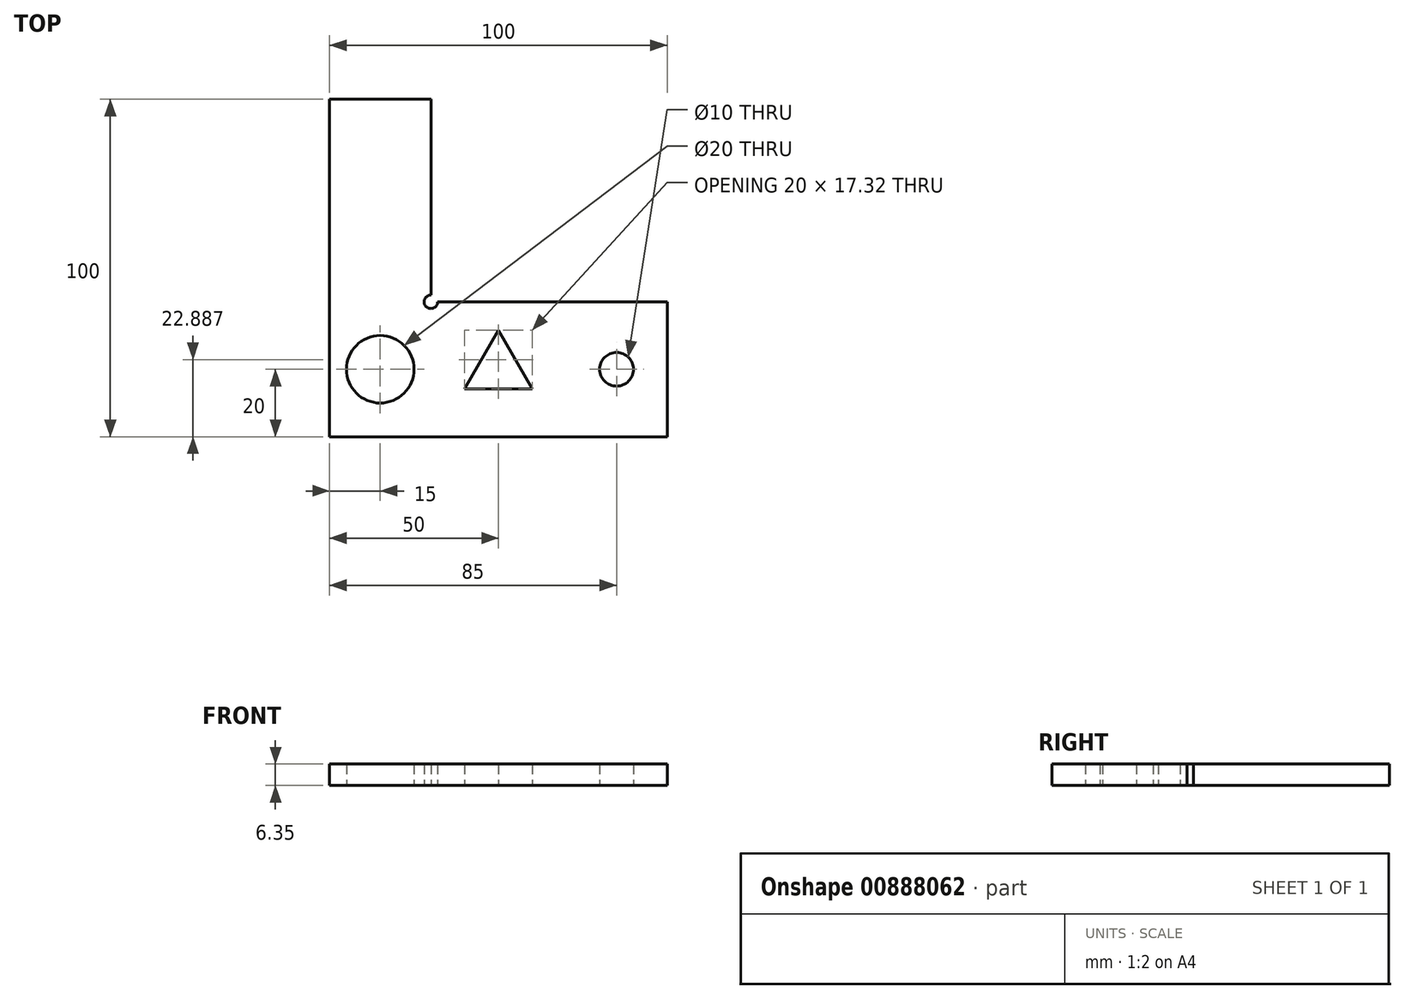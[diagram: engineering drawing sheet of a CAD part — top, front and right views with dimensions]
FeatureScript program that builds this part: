
annotation { "Feature Type Name" : "Feature", "Feature Type Description" : "" }
export const myFeature = defineFeature(function(context is Context, id is Id, definition is map)
    precondition{}
    {
        {
            var Q0;
            Q0=qCreatedBy(makeId("Top.planeOp"),FACE);
            var sketch = newSketch(context, id + "F0", { "sketchPlane" : qUnion([Q0])});
            skLineSegment(sketch, "E0", {"start": v(15, 80) * mm, "end": v(15, 22) * mm});
            skLineSegment(sketch, "E1", {"start": v(17, 20) * mm, "end": v(85, 20) * mm});
            skLineSegment(sketch, "E2", {"start": v(85, 20) * mm, "end": v(85, -20) * mm});
            skLineSegment(sketch, "E3", {"start": v(85, -20) * mm, "end": v(-15, -20) * mm});
            skLineSegment(sketch, "E4", {"start": v(-15, -20) * mm, "end": v(-15, 80) * mm});
            skLineSegment(sketch, "E5", {"start": v(-15, 80) * mm, "end": v(15, 80) * mm});
            skPoint(sketch, "E6", {"position": v(85, 0) * mm});
            skPoint(sketch, "E7", {"position": v(0, 80) * mm});
            skArc(sketch, "E8", {"start": v(17, 20) * mm, "mid": v(13.59, 18.59) * mm, "end": v(15, 22) * mm});
            skCircle(sketch, "E9", {"center": v(0, 0) * mm, "radius": 10 * mm});
            skCircle(sketch, "E10", {"center": v(70, 0) * mm, "radius": 5 * mm});
            skLineSegment(sketch, "E11", {"start": v(0, 0) * mm, "end": v(70, 0) * mm, "construction": true});
            skLineSegment(sketch, "E12", {"start": v(85, 0) * mm, "end": v(70, 0) * mm, "construction": true});
            skCircle(sketch, "E13.cCircle", {"center": v(35, 0) * mm, "radius": 5.77 * mm, "construction": true});
            skLineSegment(sketch, "E13.0", {"start": v(35, 11.55) * mm, "end": v(45, -5.77) * mm});
            skLineSegment(sketch, "E13.1", {"start": v(45, -5.77) * mm, "end": v(25, -5.77) * mm});
            skLineSegment(sketch, "E13.2", {"start": v(25, -5.77) * mm, "end": v(35, 11.55) * mm});
            skPoint(sketch, "E13.0.midPoint", {"position": v(40.77, 0) * mm});
            skSolve(sketch);
        }
        {
            var Q0;
            Q0 = qSketchRegion(id + "F0", true);
            extrude(context, id + "F1", {"entities" : qUnion([Q0]), "depth" : 6.35 * mm, "offsetDistance" : 25 * mm});
        }
    });
